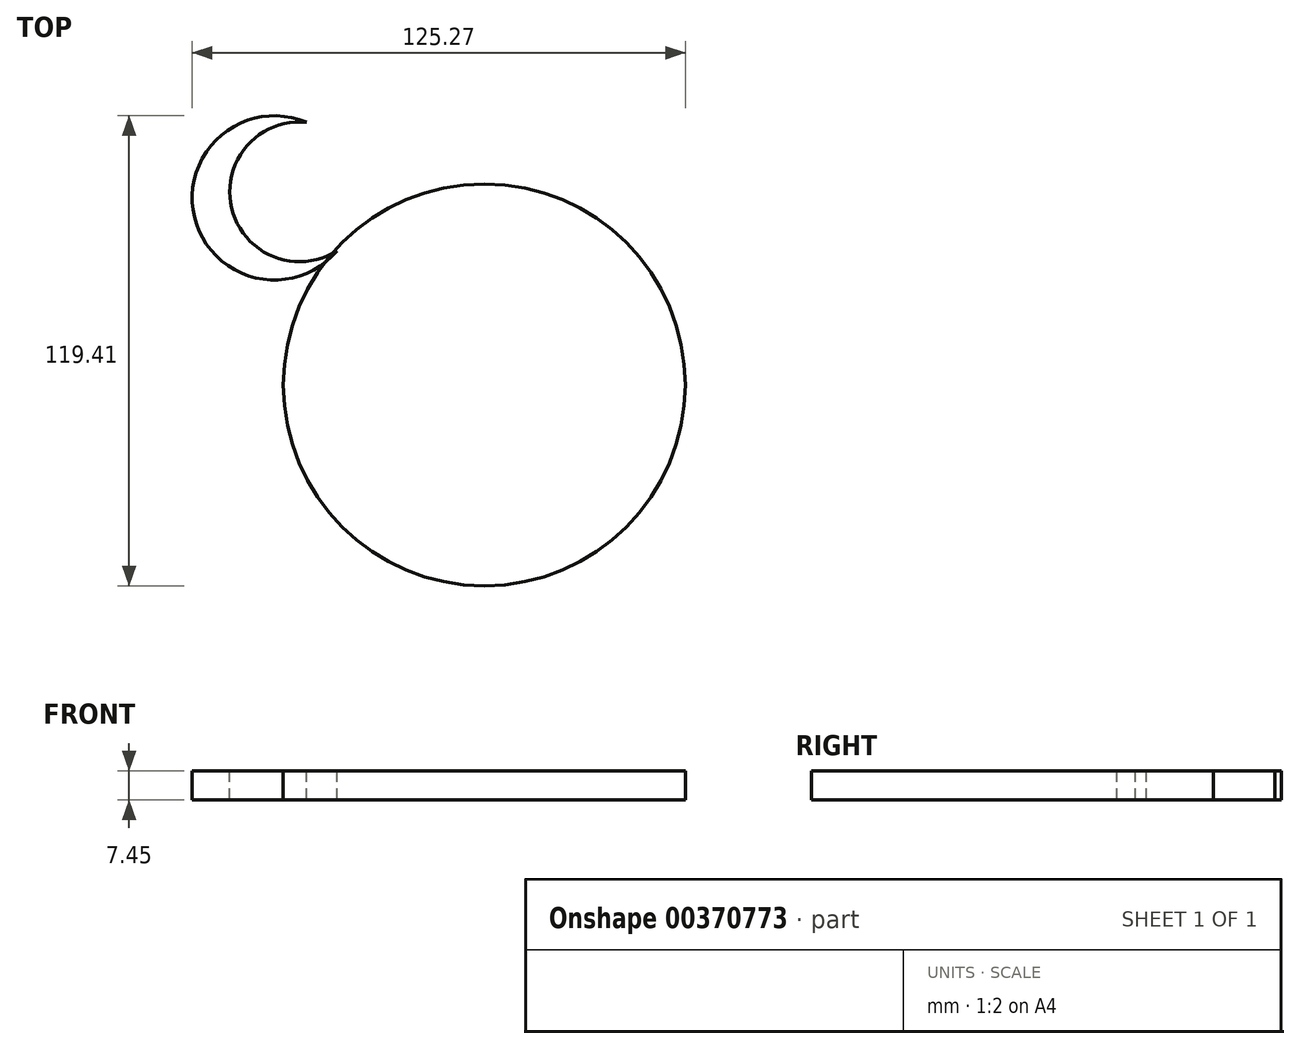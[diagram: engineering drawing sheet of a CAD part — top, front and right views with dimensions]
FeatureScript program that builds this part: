
annotation { "Feature Type Name" : "Feature", "Feature Type Description" : "" }
export const myFeature = defineFeature(function(context is Context, id is Id, definition is map)
    precondition{}
    {
        {
            var Q0;
            Q0=qCreatedBy(makeId("Top.planeOp"),FACE);
            var sketch = newSketch(context, id + "F0", { "sketchPlane" : qUnion([Q0])});
            skCircle(sketch, "E0", {"center": v(0, 0) * mm, "radius": 51.06 * mm});
            skSolve(sketch);
        }
        {
            var Q0;
            Q0=qCreatedBy(makeId("Top.planeOp"),FACE);
            var sketch = newSketch(context, id + "F1", { "sketchPlane" : qUnion([Q0])});
            skLineSegment(sketch, "E1", {"start": v(-41.12, 24.49) * mm, "end": v(-24.23, 12.64) * mm});
            skLineSegment(sketch, "E2", {"start": v(-24.23, 12.64) * mm, "end": v(-31.29, 40.63) * mm});
            skLineSegment(sketch, "E3", {"start": v(-31.29, 40.63) * mm, "end": v(-11.66, 28.48) * mm});
            skLineSegment(sketch, "E4", {"start": v(-11.66, 28.48) * mm, "end": v(-11.66, 49.68) * mm});
            skLineSegment(sketch, "E5", {"start": v(-11.66, 49.68) * mm, "end": v(17.18, 27.87) * mm});
            skLineSegment(sketch, "E6", {"start": v(17.18, 27.87) * mm, "end": v(20.13, 47.18) * mm});
            skArc(sketch, "E7", {"start": v(-45.2, 66.69) * mm, "mid": v(-62.6, 40.66) * mm, "end": v(-31.29, 40.63) * mm});
            skArc(sketch, "E8", {"start": v(-33.32, 53.32) * mm, "mid": v(-73.83, 43.5) * mm, "end": v(-32.6, 49.6) * mm});
            skSolve(sketch);
        }
        {
            var Q0;
            Q0 = qSketchRegion(id + "F0", true);
            var Q1;
            {var subQ0=sQuery(id+"F1.wireOp",EDGE,"E8");var subQ1=sQuery(id+"F1.wireOp",EDGE,"E7");var subQ2=makeQuery(id+"F1.imprint","INTERSECT",VERTEX,{"disambiguationData":[OD(0.0)],"derivedFrom":[subQ1,subQ0]});Q1=makeQuery(id+"F1.imprint","IMPRINT",FACE,{"disambiguationData":[TD([[makeQuery(id+"F1.imprint","IMPRINT",EDGE,{"disambiguationData":[TD([[subQ2,-1.0]])],"derivedFrom":subQ1}),-1.0]])]});}
            extrude(context, id + "F2", {"entities" : qUnion([Q0, Q1]), "oppositeDirection" : true, "depth" : 7.62 * mm, "hasSecondDirection" : true, "secondDirectionOppositeDirection" : true, "secondDirectionDepth" : 0.17 * mm});
        }
    });
